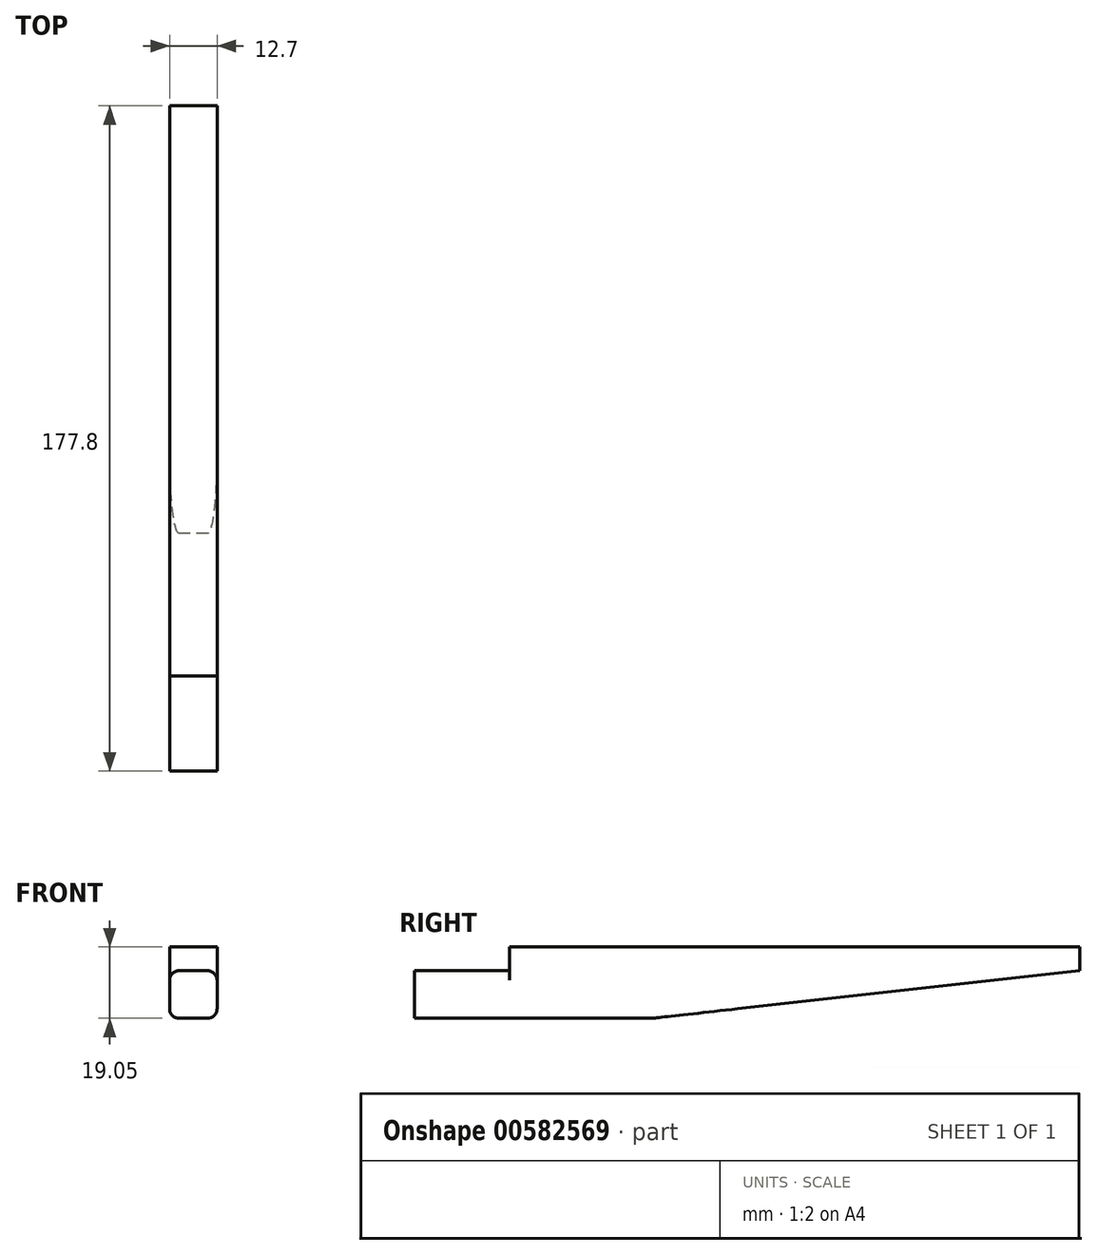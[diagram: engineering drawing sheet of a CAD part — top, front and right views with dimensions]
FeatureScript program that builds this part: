
annotation { "Feature Type Name" : "Feature", "Feature Type Description" : "" }
export const myFeature = defineFeature(function(context is Context, id is Id, definition is map)
    precondition{}
    {
        {
            var Q0;
            Q0=qCreatedBy(makeId("Right.planeOp"),FACE);
            var sketch = newSketch(context, id + "F0", { "sketchPlane" : qUnion([Q0])});
            skLineSegment(sketch, "E0", {"start": v(0, 0) * mm, "end": v(-25.4, 0) * mm});
            skLineSegment(sketch, "E1", {"start": v(0, 0) * mm, "end": v(0, 6.35) * mm});
            skLineSegment(sketch, "E2", {"start": v(0, 6.35) * mm, "end": v(152.4, 6.35) * mm});
            skLineSegment(sketch, "E3", {"start": v(152.4, 6.35) * mm, "end": v(152.4, 0) * mm});
            skLineSegment(sketch, "E4", {"start": v(152.4, 0) * mm, "end": v(38.1, -12.7) * mm});
            skLineSegment(sketch, "E5", {"start": v(38.1, -12.7) * mm, "end": v(-25.4, -12.7) * mm});
            skLineSegment(sketch, "E6", {"start": v(-25.4, -12.7) * mm, "end": v(-25.4, 0) * mm});
            skSolve(sketch);
        }
        {
            var Q0;
            Q0=makeQuery(id+"F0.imprint","IMPRINT",FACE,{"disambiguationData":[TD([[makeQuery(id+"F0.imprint","IMPRINT",EDGE,{"derivedFrom":sQuery(id+"F0.wireOp",EDGE,"E0")}),1.0]])]});
            extrude(context, id + "F1", {"entities" : qUnion([Q0]), "endBound" : BoundingType.SYMMETRIC, "depth" : 12.7 * mm, "offsetDistance" : 25.4 * mm});
        }
        {
            var Q0;
            Q0=makeQuery(id+"F1.opExtrude","CAP_EDGE",EDGE,{"disambiguationData":[OSD([sQuery(id+"F0.wireOp",EDGE,"E0")])],"isStart":false});
            var Q1;
            Q1=makeQuery(id+"F1.opExtrude","CAP_EDGE",EDGE,{"disambiguationData":[OSD([sQuery(id+"F0.wireOp",EDGE,"E0")])],"isStart":true});
            var Q2;
            Q2=makeQuery(id+"F1.opExtrude","CAP_EDGE",EDGE,{"disambiguationData":[OSD([sQuery(id+"F0.wireOp",EDGE,"E5")])],"isStart":false});
            var Q3;
            Q3=makeQuery(id+"F1.opExtrude","CAP_EDGE",EDGE,{"disambiguationData":[OSD([sQuery(id+"F0.wireOp",EDGE,"E5")])],"isStart":true});
            fillet(context, id + "F2", {"entities" : qUnion([Q0, Q1, Q2, Q3]), "radius" : 2.54 * mm, "tangentPropagation" : true, "allowEdgeOverflow" : false});
        }
    });
